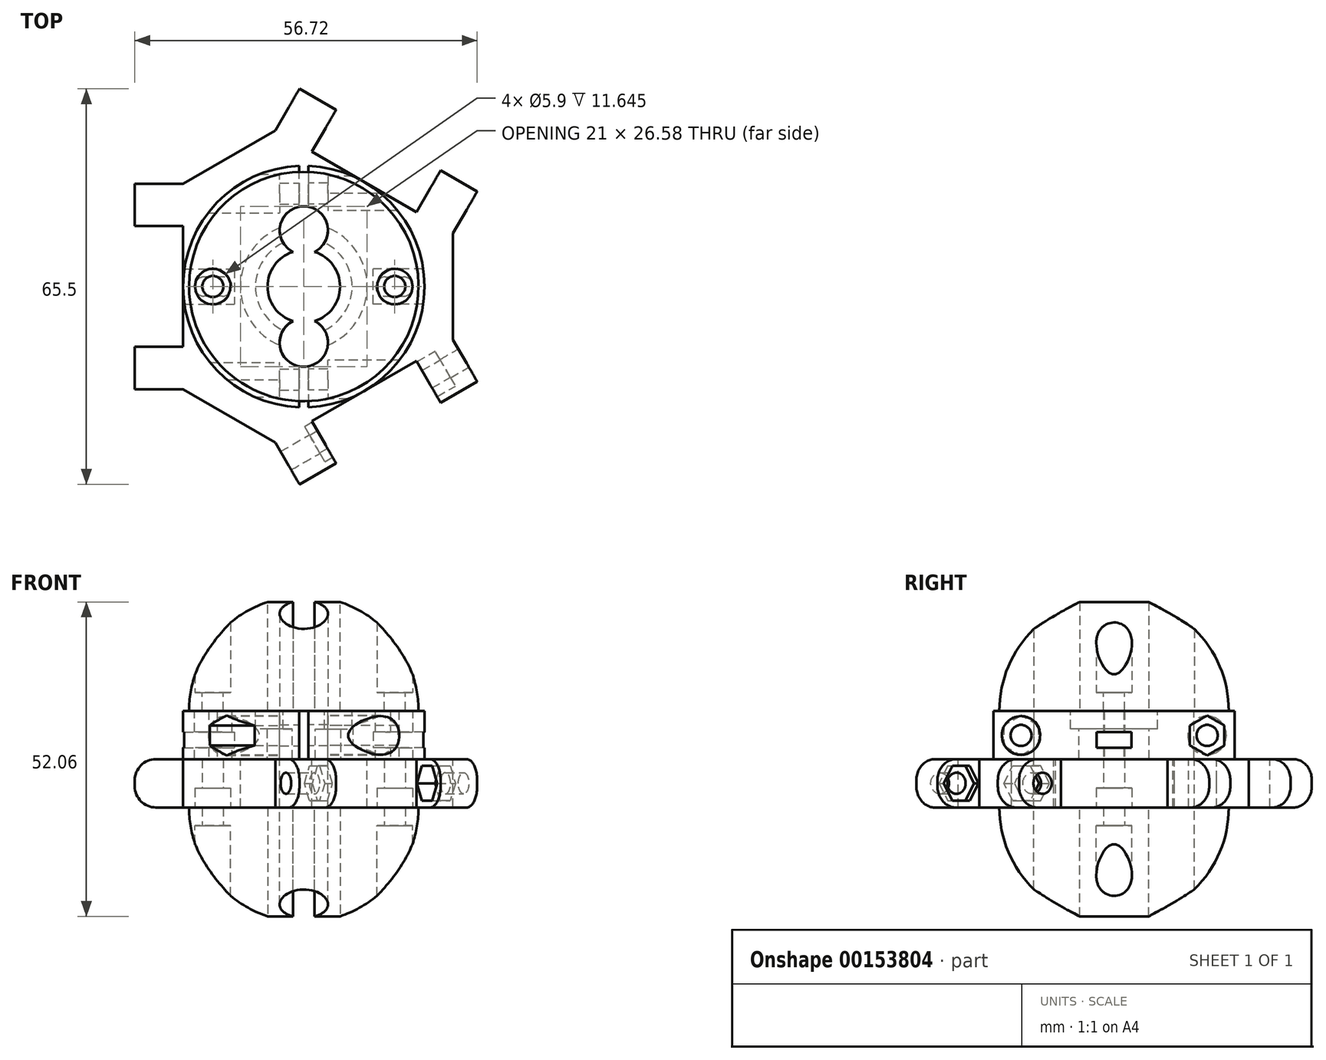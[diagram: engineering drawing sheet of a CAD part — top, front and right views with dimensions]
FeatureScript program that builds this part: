
annotation { "Feature Type Name" : "Feature", "Feature Type Description" : "" }
export const myFeature = defineFeature(function(context is Context, id is Id, definition is map)
    precondition{}
    {
        {
            var Q0;
            Q0=qCreatedBy(makeId("Top.planeOp"),FACE);
            var sketch = newSketch(context, id + "F0", { "sketchPlane" : qUnion([Q0])});
            skArc(sketch, "E0", {"start": v(0.75, -19.99) * mm, "mid": v(20, 0) * mm, "end": v(0.75, 19.99) * mm});
            skArc(sketch, "E1", {"start": v(0.75, -6.05) * mm, "mid": v(6.1, 0) * mm, "end": v(0.75, 6.05) * mm});
            skLineSegment(sketch, "E2", {"start": v(0.75, 19.99) * mm, "end": v(0.75, 6.05) * mm});
            skLineSegment(sketch, "E3.trimOffspring", {"start": v(0.75, -6.05) * mm, "end": v(0.75, -19.99) * mm});
            skSolve(sketch);
        }
        {
            var Q0;
            Q0 = qSketchRegion(id + "F0", true);
            extrude(context, id + "F1", {"entities" : qUnion([Q0]), "depth" : 8 * mm});
        }
        {
            var Q0;
            Q0=qCreatedBy(makeId("Top.planeOp"),FACE);
            cPlane(context, id + "F2", {"entities" : qUnion([Q0]), "cplaneType" : CPlaneType.OFFSET, "offset" : 5 * mm, "width" : 150 * mm, "height" : 150 * mm});
        }
        {
            var Q0;
            Q0=makeQuery(id+"F1.opExtrude","CAP_FACE",FACE,{"disambiguationData":[OSD([sQuery(id+"F0.wireOp",EDGE,"E0"),sQuery(id+"F0.wireOp",EDGE,"E1"),sQuery(id+"F0.wireOp",EDGE,"E2"),sQuery(id+"F0.wireOp",EDGE,"E3.trimOffspring")])],"isStart":false});
            var sketch = newSketch(context, id + "F3", { "sketchPlane" : qUnion([Q0])});
            skCircle(sketch, "E4", {"center": v(0, 0) * mm, "radius": 8 * mm});
            skSolve(sketch);
        }
        {
            var Q0;
            Q0 = qSketchRegion(id + "F3", true);
            var Q1;
            Q1=qCreatedBy(id+"F2.planeOp",FACE);
            extrude(context, id + "F4", {"entities" : qUnion([Q0]), "operationType" : NewBodyOperationType.REMOVE, "endBound" : BoundingType.UP_TO_SURFACE, "oppositeDirection" : true, "endBoundEntityFace" : qUnion([Q1]), "depth" : 25 * mm});
        }
        {
            var Q0;
            Q0=makeQuery(id+"F1.opExtrude","SWEPT_FACE",FACE,{"disambiguationData":[OSD([sQuery(id+"F0.wireOp",EDGE,"E3.trimOffspring")])]});
            var sketch = newSketch(context, id + "F5", { "sketchPlane" : qUnion([Q0])});
            skCircle(sketch, "E5", {"center": v(-15.4, 3.92) * mm, "radius": 1.75 * mm});
            skLineSegment(sketch, "E6", {"start": v(-22.4, 7.85) * mm, "end": v(-22.4, 0) * mm, "construction": true});
            skLineSegment(sketch, "E7", {"start": v(-22.4, 0) * mm, "end": v(-22.4, 3.92) * mm, "construction": true});
            skLineSegment(sketch, "E8", {"start": v(-22.4, 3.92) * mm, "end": v(-12.2, 3.92) * mm, "construction": true});
            skCircle(sketch, "E9.MirrorC", {"center": v(15.4, 3.92) * mm, "radius": 1.75 * mm});
            skSolve(sketch);
        }
        {
            var Q0;
            Q0 = qSketchRegion(id + "F5", true);
            extrude(context, id + "F6", {"entities" : qUnion([Q0]), "operationType" : NewBodyOperationType.REMOVE, "endBound" : BoundingType.UP_TO_NEXT, "oppositeDirection" : true, "depth" : 25 * mm});
        }
        {
            var Q0;
            Q0=qCreatedBy(makeId("Right.planeOp"),FACE);
            cPlane(context, id + "F7", {"entities" : qUnion([Q0]), "cplaneType" : CPlaneType.OFFSET, "offset" : 4 * mm, "width" : 150 * mm, "height" : 150 * mm});
        }
        {
            var Q0;
            Q0=qCreatedBy(id+"F7.planeOp",FACE);
            var sketch = newSketch(context, id + "F8", { "sketchPlane" : qUnion([Q0])});
            skCircle(sketch, "E10.cCircle", {"center": v(15.4, 3.92) * mm, "radius": 3.3 * mm, "construction": true});
            skLineSegment(sketch, "E10.0", {"start": v(12.55, 2.27) * mm, "end": v(12.55, 5.57) * mm});
            skLineSegment(sketch, "E10.1", {"start": v(12.55, 5.57) * mm, "end": v(15.4, 7.22) * mm});
            skLineSegment(sketch, "E10.2", {"start": v(15.4, 7.22) * mm, "end": v(18.27, 5.57) * mm});
            skLineSegment(sketch, "E10.3", {"start": v(18.27, 5.57) * mm, "end": v(18.27, 2.27) * mm});
            skLineSegment(sketch, "E10.4", {"start": v(18.27, 2.27) * mm, "end": v(15.4, 0.62) * mm});
            skLineSegment(sketch, "E10.5", {"start": v(15.4, 0.62) * mm, "end": v(12.55, 2.27) * mm});
            skCircle(sketch, "E11", {"center": v(-15.4, 3.92) * mm, "radius": 3.2 * mm});
            skSolve(sketch);
        }
        {
            var Q0;
            Q0 = qSketchRegion(id + "F8", true);
            var Q1;
            Q1=makeQuery(id+"F1.opExtrude","SWEPT_FACE",FACE,{"disambiguationData":[OSD([sQuery(id+"F0.wireOp",EDGE,"E0")])]});
            extrude(context, id + "F9", {"entities" : qUnion([Q0]), "operationType" : NewBodyOperationType.REMOVE, "endBound" : BoundingType.UP_TO_SURFACE, "endBoundEntityFace" : qUnion([Q1]), "depth" : 25 * mm});
        }
        {
            var Q0;
            {var subQ5=makeQuery(id+"F1.opExtrude","CAP_EDGE",EDGE,{"disambiguationData":[OSD([sQuery(id+"F0.wireOp",EDGE,"E0")])],"isStart":false});Q0=makeQuery(id+"F3.imprint","IMPRINT",FACE,{"disambiguationData":[TD([[makeQuery(id+"F3.imprint","IMPRINT",EDGE,{"derivedFrom":subQ5}),1.0]])]});}
            var sketch = newSketch(context, id + "F10", { "sketchPlane" : qUnion([Q0])});
            skLineSegment(sketch, "E12.bottom", {"start": v(16.5, 1.6) * mm, "end": v(13.5, 1.6) * mm});
            skLineSegment(sketch, "E12.top", {"start": v(16.5, -1.6) * mm, "end": v(13.5, -1.6) * mm});
            skPoint(sketch, "E12.middle", {"position": v(15, 0) * mm});
            skArc(sketch, "E13", {"start": v(16.5, -1.6) * mm, "mid": v(18.1, 0) * mm, "end": v(16.5, 1.6) * mm});
            skArc(sketch, "E14", {"start": v(13.5, 1.6) * mm, "mid": v(11.9, 0) * mm, "end": v(13.5, -1.6) * mm});
            skSolve(sketch);
        }
        {
            var Q0;
            Q0 = qSketchRegion(id + "F10", true);
            extrude(context, id + "F11", {"entities" : qUnion([Q0]), "operationType" : NewBodyOperationType.REMOVE, "endBound" : BoundingType.UP_TO_NEXT, "oppositeDirection" : true, "depth" : 25 * mm});
        }
        {
            var Q0;
            Q0=qCreatedBy(makeId("Right.planeOp"),FACE);
            cPlane(context, id + "F12", {"entities" : qUnion([Q0]), "cplaneType" : CPlaneType.OFFSET, "offset" : 11.5 * mm, "width" : 150 * mm, "height" : 150 * mm});
        }
        {
            var Q0;
            Q0=qCreatedBy(id+"F12.planeOp",FACE);
            var sketch = newSketch(context, id + "F13", { "sketchPlane" : qUnion([Q0])});
            skLineSegment(sketch, "E15.bottom", {"start": v(-2.9, 4.5) * mm, "end": v(2.9, 4.5) * mm});
            skLineSegment(sketch, "E15.top", {"start": v(-2.9, 1.9) * mm, "end": v(2.9, 1.9) * mm});
            skLineSegment(sketch, "E15.left", {"start": v(-2.9, 4.5) * mm, "end": v(-2.9, 1.9) * mm});
            skLineSegment(sketch, "E15.right", {"start": v(2.9, 4.5) * mm, "end": v(2.9, 1.9) * mm});
            skPoint(sketch, "E15.middle", {"position": v(0, 3.2) * mm});
            skSolve(sketch);
        }
        {
            var Q0;
            Q0 = qSketchRegion(id + "F13", true);
            var Q1;
            Q1=makeQuery(id+"F1.opExtrude","SWEPT_FACE",FACE,{"disambiguationData":[OSD([sQuery(id+"F0.wireOp",EDGE,"E0")])]});
            extrude(context, id + "F14", {"entities" : qUnion([Q0]), "operationType" : NewBodyOperationType.REMOVE, "endBound" : BoundingType.UP_TO_SURFACE, "endBoundEntityFace" : qUnion([Q1]), "depth" : 25 * mm});
        }
        {
            var Q0;
            Q0=qCreatedBy(makeId("Right.planeOp"),FACE);
            var sketch = newSketch(context, id + "F15", { "sketchPlane" : qUnion([Q0])});
            skLineSegment(sketch, "E16", {"start": v(0, 0) * mm, "end": v(0, 20.2) * mm, "construction": true});
            skSolve(sketch);
        }
        {
            var Q0;
            Q0=makeQuery(id+"F1.opExtrude","SWEPT_BODY",BODY,{"disambiguationData":[OSD([sQuery(id+"F0.wireOp",EDGE,"E0"),sQuery(id+"F0.wireOp",EDGE,"E1"),sQuery(id+"F0.wireOp",EDGE,"E2"),sQuery(id+"F0.wireOp",EDGE,"E3.trimOffspring")])]});
            var Q1;
            Q1=sQuery(id+"F15.wireOp",EDGE,"E16");
            transform(context, id + "F16", {"entities" : qUnion([Q0]), "transformType" : TransformType.ROTATION, "transformAxis" : qUnion([Q1]), "angle" : 180 * degree, "makeCopy" : true});
        }
        {
            var Q0;
            Q0=makeQuery(id+"F16.opPattern","COPY",FACE,{"derivedFrom":makeQuery(id+"F1.opExtrude","CAP_FACE",FACE,{"disambiguationData":[OSD([sQuery(id+"F0.wireOp",EDGE,"E0"),sQuery(id+"F0.wireOp",EDGE,"E1"),sQuery(id+"F0.wireOp",EDGE,"E2"),sQuery(id+"F0.wireOp",EDGE,"E3.trimOffspring")])],"isStart":true}),"instanceName":"1"});
            var sketch = newSketch(context, id + "F17", { "sketchPlane" : qUnion([Q0])});
            skCircle(sketch, "E17.cCircle", {"center": v(0, 0) * mm, "radius": 24.72 * mm, "construction": true});
            skLineSegment(sketch, "E17.0", {"start": v(17, 20) * mm, "end": v(25.82, 4.72) * mm});
            skLineSegment(sketch, "E17.1", {"start": v(8.82, -24.72) * mm, "end": v(-8.82, -24.72) * mm});
            skLineSegment(sketch, "E17.2", {"start": v(-25.82, 4.72) * mm, "end": v(-17, 20) * mm});
            skPoint(sketch, "E17.0.midPoint", {"position": v(21.41, 12.36) * mm});
            skCircle(sketch, "E18", {"center": v(0, 0) * mm, "radius": 10.5 * mm});
            skLineSegment(sketch, "E19", {"start": v(-10, 20) * mm, "end": v(10, 20) * mm});
            skPoint(sketch, "E20.orphan", {"position": v(0, 49.44) * mm});
            skPoint(sketch, "E21.orphan", {"position": v(42.82, -24.72) * mm});
            skPoint(sketch, "E22.orphan", {"position": v(-42.82, -24.72) * mm});
            skLineSegment(sketch, "E23.top", {"start": v(-17, 28) * mm, "end": v(-10, 28) * mm});
            skLineSegment(sketch, "E23.left", {"start": v(-17, 20) * mm, "end": v(-17, 28) * mm});
            skLineSegment(sketch, "E23.right", {"start": v(-10, 20) * mm, "end": v(-10, 28) * mm});
            skLineSegment(sketch, "E24.top", {"start": v(17, 28) * mm, "end": v(10, 28) * mm});
            skLineSegment(sketch, "E24.left", {"start": v(17, 20) * mm, "end": v(17, 28) * mm});
            skLineSegment(sketch, "E24.right", {"start": v(10, 20) * mm, "end": v(10, 28) * mm});
            skPoint(sketch, "E25.center", {"position": v(0, -1.44) * mm});
            skLineSegment(sketch, "E26.1.0", {"start": v(-8.82, -24.72) * mm, "end": v(-15.75, -28.72) * mm});
            skLineSegment(sketch, "E26.1.1", {"start": v(-15.75, -28.72) * mm, "end": v(-19.25, -22.66) * mm});
            skLineSegment(sketch, "E26.1.2", {"start": v(-12.32, -18.66) * mm, "end": v(-19.25, -22.66) * mm});
            skLineSegment(sketch, "E26.1.3", {"start": v(-22.32, -1.34) * mm, "end": v(-29.25, -5.34) * mm});
            skLineSegment(sketch, "E26.1.4", {"start": v(-32.75, 0.72) * mm, "end": v(-29.25, -5.34) * mm});
            skLineSegment(sketch, "E26.1.5", {"start": v(-25.82, 4.72) * mm, "end": v(-32.75, 0.72) * mm});
            skLineSegment(sketch, "E26.2.0", {"start": v(25.82, 4.72) * mm, "end": v(32.75, 0.72) * mm});
            skLineSegment(sketch, "E26.2.1", {"start": v(32.75, 0.72) * mm, "end": v(29.25, -5.34) * mm});
            skLineSegment(sketch, "E26.2.2", {"start": v(22.32, -1.34) * mm, "end": v(29.25, -5.34) * mm});
            skLineSegment(sketch, "E26.2.3", {"start": v(12.32, -18.66) * mm, "end": v(19.25, -22.66) * mm});
            skLineSegment(sketch, "E26.2.4", {"start": v(15.75, -28.72) * mm, "end": v(19.25, -22.66) * mm});
            skLineSegment(sketch, "E26.2.5", {"start": v(8.82, -24.72) * mm, "end": v(15.75, -28.72) * mm});
            skLineSegment(sketch, "E27.trimOffspring", {"start": v(-22.32, -1.34) * mm, "end": v(-12.32, -18.66) * mm});
            skLineSegment(sketch, "E28.trimOffspring", {"start": v(22.32, -1.34) * mm, "end": v(12.32, -18.66) * mm});
            skSolve(sketch);
        }
        {
            var Q0;
            Q0 = qSketchRegion(id + "F17", true);
            extrude(context, id + "F18", {"entities" : qUnion([Q0]), "depth" : 8 * mm});
        }
        {
            var Q0;
            Q0=makeQuery(id+"F18.opExtrude","CAP_EDGE",EDGE,{"disambiguationData":[OSD([sQuery(id+"F17.wireOp",EDGE,"E26.2.1")])],"isStart":false});
            var Q1;
            Q1=makeQuery(id+"F18.opExtrude","CAP_EDGE",EDGE,{"disambiguationData":[OSD([sQuery(id+"F17.wireOp",EDGE,"E26.2.1")])],"isStart":true});
            var Q2;
            Q2=makeQuery(id+"F18.opExtrude","CAP_EDGE",EDGE,{"disambiguationData":[OSD([sQuery(id+"F17.wireOp",EDGE,"E26.2.4")])],"isStart":false});
            var Q3;
            Q3=makeQuery(id+"F18.opExtrude","CAP_EDGE",EDGE,{"disambiguationData":[OSD([sQuery(id+"F17.wireOp",EDGE,"E26.2.4")])],"isStart":true});
            var Q4;
            Q4=makeQuery(id+"F18.opExtrude","CAP_EDGE",EDGE,{"disambiguationData":[OSD([sQuery(id+"F17.wireOp",EDGE,"E26.1.1")])],"isStart":false});
            var Q5;
            Q5=makeQuery(id+"F18.opExtrude","CAP_EDGE",EDGE,{"disambiguationData":[OSD([sQuery(id+"F17.wireOp",EDGE,"E26.1.1")])],"isStart":true});
            var Q6;
            Q6=makeQuery(id+"F18.opExtrude","CAP_EDGE",EDGE,{"disambiguationData":[OSD([sQuery(id+"F17.wireOp",EDGE,"E26.1.4")])],"isStart":false});
            var Q7;
            Q7=makeQuery(id+"F18.opExtrude","CAP_EDGE",EDGE,{"disambiguationData":[OSD([sQuery(id+"F17.wireOp",EDGE,"E26.1.4")])],"isStart":true});
            var Q8;
            Q8=makeQuery(id+"F18.opExtrude","CAP_EDGE",EDGE,{"disambiguationData":[OSD([sQuery(id+"F17.wireOp",EDGE,"E23.top")])],"isStart":false});
            var Q9;
            Q9=makeQuery(id+"F18.opExtrude","CAP_EDGE",EDGE,{"disambiguationData":[OSD([sQuery(id+"F17.wireOp",EDGE,"E24.top")])],"isStart":false});
            var Q10;
            Q10=makeQuery(id+"F18.opExtrude","CAP_EDGE",EDGE,{"disambiguationData":[OSD([sQuery(id+"F17.wireOp",EDGE,"E23.top")])],"isStart":true});
            var Q11;
            Q11=makeQuery(id+"F18.opExtrude","CAP_EDGE",EDGE,{"disambiguationData":[OSD([sQuery(id+"F17.wireOp",EDGE,"E24.top")])],"isStart":true});
            fillet(context, id + "F19", {"entities" : qUnion([Q0, Q1, Q2, Q3, Q4, Q5, Q6, Q7, Q8, Q9, Q10, Q11]), "radius" : 3.5 * mm, "allowEdgeOverflow" : false});
        }
        {
            var Q0;
            Q0=qCreatedBy(makeId("Front.planeOp"),FACE);
            var sketch = newSketch(context, id + "F20", { "sketchPlane" : qUnion([Q0])});
            skLineSegment(sketch, "E29", {"start": v(0, 0) * mm, "end": v(0, 34.14) * mm, "construction": true});
            skSolve(sketch);
        }
        {
            var Q0;
            Q0=makeQuery(id+"F18.opExtrude","SWEPT_BODY",BODY,{"disambiguationData":[OSD([sQuery(id+"F17.wireOp",EDGE,"E17.0"),sQuery(id+"F17.wireOp",EDGE,"E17.1"),sQuery(id+"F17.wireOp",EDGE,"E17.2"),sQuery(id+"F17.wireOp",EDGE,"E18"),sQuery(id+"F17.wireOp",EDGE,"E19"),sQuery(id+"F17.wireOp",EDGE,"E23.top"),sQuery(id+"F17.wireOp",EDGE,"E23.left"),sQuery(id+"F17.wireOp",EDGE,"E23.right"),sQuery(id+"F17.wireOp",EDGE,"E24.top"),sQuery(id+"F17.wireOp",EDGE,"E24.left"),sQuery(id+"F17.wireOp",EDGE,"E24.right"),sQuery(id+"F17.wireOp",EDGE,"E26.1.0"),sQuery(id+"F17.wireOp",EDGE,"E26.1.1"),sQuery(id+"F17.wireOp",EDGE,"E26.1.2"),sQuery(id+"F17.wireOp",EDGE,"E26.1.3"),sQuery(id+"F17.wireOp",EDGE,"E26.1.4"),sQuery(id+"F17.wireOp",EDGE,"E26.1.5"),sQuery(id+"F17.wireOp",EDGE,"E26.2.0"),sQuery(id+"F17.wireOp",EDGE,"E26.2.1"),sQuery(id+"F17.wireOp",EDGE,"E26.2.2"),sQuery(id+"F17.wireOp",EDGE,"E26.2.3"),sQuery(id+"F17.wireOp",EDGE,"E26.2.4"),sQuery(id+"F17.wireOp",EDGE,"E26.2.5"),sQuery(id+"F17.wireOp",EDGE,"E27.trimOffspring"),sQuery(id+"F17.wireOp",EDGE,"E28.trimOffspring")])]});
            var Q1;
            Q1=sQuery(id+"F20.wireOp",EDGE,"E29");
            transform(context, id + "F21", {"entities" : qUnion([Q0]), "transformType" : TransformType.ROTATION, "transformAxis" : qUnion([Q1]), "angle" : 30 * degree, "makeCopy" : false});
        }
        {
            var Q0;
            Q0=makeQuery(id+"F18.opExtrude","SWEPT_FACE",FACE,{"disambiguationData":[OSD([sQuery(id+"F17.wireOp",EDGE,"E24.left")])]});
            var sketch = newSketch(context, id + "F22", { "sketchPlane" : qUnion([Q0])});
            skPoint(sketch, "E30", {"position": v(-20, -4) * mm});
            skCircle(sketch, "E31", {"center": v(-23.5, -4) * mm, "radius": 1.75 * mm});
            skSolve(sketch);
        }
        {
            var Q0;
            Q0 = qSketchRegion(id + "F22", true);
            var Q1;
            Q1=sQuery(id+"F22.wireOp",EDGE,"E31");
            extrude(context, id + "F23", {"entities" : qUnion([Q0]), "operationType" : NewBodyOperationType.REMOVE, "surfaceEntities" : qUnion([Q1]), "endBound" : BoundingType.THROUGH_ALL, "oppositeDirection" : true, "depth" : 25 * mm});
        }
        {
            var Q0;
            Q0=makeQuery(id+"F18.opExtrude","SWEPT_FACE",FACE,{"disambiguationData":[OSD([sQuery(id+"F17.wireOp",EDGE,"E24.right")])]});
            cPlane(context, id + "F24", {"entities" : qUnion([Q0]), "cplaneType" : CPlaneType.OFFSET, "offset" : 3.5 * mm, "oppositeDirection" : true, "width" : 150 * mm, "height" : 150 * mm});
        }
        {
            var Q0;
            Q0=qCreatedBy(id+"F24.planeOp",FACE);
            var sketch = newSketch(context, id + "F25", { "sketchPlane" : qUnion([Q0])});
            skCircle(sketch, "E32.cCircle", {"center": v(23.5, -4) * mm, "radius": 2.9 * mm, "construction": true});
            skLineSegment(sketch, "E32.0", {"start": v(26.84, -4) * mm, "end": v(25.16, -6.9) * mm});
            skLineSegment(sketch, "E32.1", {"start": v(25.16, -6.9) * mm, "end": v(21.82, -6.9) * mm});
            skLineSegment(sketch, "E32.2", {"start": v(21.82, -6.9) * mm, "end": v(20.14, -4) * mm});
            skLineSegment(sketch, "E32.3", {"start": v(20.14, -4) * mm, "end": v(21.82, -1.1) * mm});
            skLineSegment(sketch, "E32.4", {"start": v(21.82, -1.1) * mm, "end": v(25.16, -1.1) * mm});
            skLineSegment(sketch, "E32.5", {"start": v(25.16, -1.1) * mm, "end": v(26.84, -4) * mm});
            skPoint(sketch, "E32.0.midPoint", {"position": v(26, -5.45) * mm});
            skSolve(sketch);
        }
        {
            var Q0;
            Q0 = qSketchRegion(id + "F25", true);
            extrude(context, id + "F26", {"entities" : qUnion([Q0]), "operationType" : NewBodyOperationType.REMOVE, "depth" : 25 * mm});
        }
        {
            var Q0;
            Q0=makeQuery(id+"F18.opExtrude","CAP_FACE",FACE,{"disambiguationData":[OSD([sQuery(id+"F17.wireOp",EDGE,"E17.0"),sQuery(id+"F17.wireOp",EDGE,"E17.1"),sQuery(id+"F17.wireOp",EDGE,"E17.2"),sQuery(id+"F17.wireOp",EDGE,"E18"),sQuery(id+"F17.wireOp",EDGE,"E19"),sQuery(id+"F17.wireOp",EDGE,"E23.top"),sQuery(id+"F17.wireOp",EDGE,"E23.left"),sQuery(id+"F17.wireOp",EDGE,"E23.right"),sQuery(id+"F17.wireOp",EDGE,"E24.top"),sQuery(id+"F17.wireOp",EDGE,"E24.left"),sQuery(id+"F17.wireOp",EDGE,"E24.right"),sQuery(id+"F17.wireOp",EDGE,"E26.1.0"),sQuery(id+"F17.wireOp",EDGE,"E26.1.1"),sQuery(id+"F17.wireOp",EDGE,"E26.1.2"),sQuery(id+"F17.wireOp",EDGE,"E26.1.3"),sQuery(id+"F17.wireOp",EDGE,"E26.1.4"),sQuery(id+"F17.wireOp",EDGE,"E26.1.5"),sQuery(id+"F17.wireOp",EDGE,"E26.2.0"),sQuery(id+"F17.wireOp",EDGE,"E26.2.1"),sQuery(id+"F17.wireOp",EDGE,"E26.2.2"),sQuery(id+"F17.wireOp",EDGE,"E26.2.3"),sQuery(id+"F17.wireOp",EDGE,"E26.2.4"),sQuery(id+"F17.wireOp",EDGE,"E26.2.5"),sQuery(id+"F17.wireOp",EDGE,"E27.trimOffspring"),sQuery(id+"F17.wireOp",EDGE,"E28.trimOffspring")])],"isStart":false});
            var sketch = newSketch(context, id + "F27", { "sketchPlane" : qUnion([Q0])});
            skPoint(sketch, "E33", {"position": v(-15.06, 0) * mm});
            skPoint(sketch, "E34.MirrorP", {"position": v(15.06, 0) * mm});
            skSolve(sketch);
        }
        {
            var Q0;
            Q0=sQuery(id+"F27.wireOp",VERTEX,"E34.MirrorP");
            var Q1;
            Q1=sQuery(id+"F27.wireOp",VERTEX,"E33");
            var Q2;
            Q2=makeQuery(id+"F18.opExtrude","SWEPT_BODY",BODY,{"disambiguationData":[OSD([sQuery(id+"F17.wireOp",EDGE,"E17.0"),sQuery(id+"F17.wireOp",EDGE,"E17.1"),sQuery(id+"F17.wireOp",EDGE,"E17.2"),sQuery(id+"F17.wireOp",EDGE,"E18"),sQuery(id+"F17.wireOp",EDGE,"E19"),sQuery(id+"F17.wireOp",EDGE,"E23.top"),sQuery(id+"F17.wireOp",EDGE,"E23.left"),sQuery(id+"F17.wireOp",EDGE,"E23.right"),sQuery(id+"F17.wireOp",EDGE,"E24.top"),sQuery(id+"F17.wireOp",EDGE,"E24.left"),sQuery(id+"F17.wireOp",EDGE,"E24.right"),sQuery(id+"F17.wireOp",EDGE,"E26.1.0"),sQuery(id+"F17.wireOp",EDGE,"E26.1.1"),sQuery(id+"F17.wireOp",EDGE,"E26.1.2"),sQuery(id+"F17.wireOp",EDGE,"E26.1.3"),sQuery(id+"F17.wireOp",EDGE,"E26.1.4"),sQuery(id+"F17.wireOp",EDGE,"E26.1.5"),sQuery(id+"F17.wireOp",EDGE,"E26.2.0"),sQuery(id+"F17.wireOp",EDGE,"E26.2.1"),sQuery(id+"F17.wireOp",EDGE,"E26.2.2"),sQuery(id+"F17.wireOp",EDGE,"E26.2.3"),sQuery(id+"F17.wireOp",EDGE,"E26.2.4"),sQuery(id+"F17.wireOp",EDGE,"E26.2.5"),sQuery(id+"F17.wireOp",EDGE,"E27.trimOffspring"),sQuery(id+"F17.wireOp",EDGE,"E28.trimOffspring")])]});
            hole(context, id + "F28", {"style" : HoleStyle.C_BORE, "endStyle" : HoleEndStyle.THROUGH, "holeDiameter" : 3.5 * mm, "cBoreDiameter" : 5.9 * mm, "cBoreDepth" : 3.2 * mm, "locations" : qUnion([Q0, Q1]), "scope" : qUnion([Q2]), "isTappedThrough" : true});
        }
        {
            var Q0;
            Q0=sQuery(id+"F20.wireOp",EDGE,"E29");
            cPlane(context, id + "F29", {"entities" : qUnion([Q0]), "cplaneType" : CPlaneType.LINE_ANGLE, "offset" : 25 * mm, "angle" : 0 * degree, "width" : 150 * mm, "height" : 150 * mm});
        }
        {
            var Q0;
            Q0=qCreatedBy(id+"F29.planeOp",FACE);
            var sketch = newSketch(context, id + "F30", { "sketchPlane" : qUnion([Q0])});
            skPoint(sketch, "E35", {"position": v(-19, -8) * mm});
            skArc(sketch, "E36", {"start": v(-19, -8) * mm, "mid": v(-15.41, -19.11) * mm, "end": v(-6, -26.03) * mm});
            skLineSegment(sketch, "E37", {"start": v(-19, -8) * mm, "end": v(-6, -8) * mm});
            skLineSegment(sketch, "E38", {"start": v(-6, -8) * mm, "end": v(-6, -26.03) * mm});
            skSolve(sketch);
        }
        {
            var Q0;
            Q0 = qSketchRegion(id + "F30", true);
            var Q1;
            Q1=sQuery(id+"F20.wireOp",EDGE,"E29");
            revolve(context, id + "F31", {"entities" : qUnion([Q0]), "axis" : qUnion([Q1]), "revolveType" : RevolveType.FULL});
        }
        {
            var Q0;
            {var subQ5=makeQuery(id+"F1.opExtrude","CAP_EDGE",EDGE,{"disambiguationData":[OSD([sQuery(id+"F0.wireOp",EDGE,"E1")])],"isStart":false});Q0=makeQuery(id+"F3.imprint","IMPRINT",FACE,{"disambiguationData":[TD([[makeQuery(id+"F3.imprint","IMPRINT",EDGE,{"derivedFrom":subQ5}),1.0]])]});}
            var sketch = newSketch(context, id + "F32", { "sketchPlane" : qUnion([Q0])});
            skCircle(sketch, "E39", {"center": v(0, 9.3) * mm, "radius": 4 * mm});
            skLineSegment(sketch, "E40", {"start": v(0, 0) * mm, "end": v(-36.82, 0) * mm, "construction": true});
            skCircle(sketch, "E41.MirrorC", {"center": v(0, -9.3) * mm, "radius": 4 * mm});
            skSolve(sketch);
        }
        {
            var Q0;
            Q0 = qSketchRegion(id + "F32", true);
            extrude(context, id + "F33", {"entities" : qUnion([Q0]), "operationType" : NewBodyOperationType.REMOVE, "endBound" : BoundingType.THROUGH_ALL, "oppositeDirection" : true, "depth" : 25 * mm});
        }
        {
            var Q0;
            Q0=makeQuery(id+"F18.opExtrude","CAP_FACE",FACE,{"disambiguationData":[OSD([sQuery(id+"F17.wireOp",EDGE,"E17.0"),sQuery(id+"F17.wireOp",EDGE,"E17.1"),sQuery(id+"F17.wireOp",EDGE,"E17.2"),sQuery(id+"F17.wireOp",EDGE,"E18"),sQuery(id+"F17.wireOp",EDGE,"E19"),sQuery(id+"F17.wireOp",EDGE,"E23.top"),sQuery(id+"F17.wireOp",EDGE,"E23.left"),sQuery(id+"F17.wireOp",EDGE,"E23.right"),sQuery(id+"F17.wireOp",EDGE,"E24.top"),sQuery(id+"F17.wireOp",EDGE,"E24.left"),sQuery(id+"F17.wireOp",EDGE,"E24.right"),sQuery(id+"F17.wireOp",EDGE,"E26.1.0"),sQuery(id+"F17.wireOp",EDGE,"E26.1.1"),sQuery(id+"F17.wireOp",EDGE,"E26.1.2"),sQuery(id+"F17.wireOp",EDGE,"E26.1.3"),sQuery(id+"F17.wireOp",EDGE,"E26.1.4"),sQuery(id+"F17.wireOp",EDGE,"E26.1.5"),sQuery(id+"F17.wireOp",EDGE,"E26.2.0"),sQuery(id+"F17.wireOp",EDGE,"E26.2.1"),sQuery(id+"F17.wireOp",EDGE,"E26.2.2"),sQuery(id+"F17.wireOp",EDGE,"E26.2.3"),sQuery(id+"F17.wireOp",EDGE,"E26.2.4"),sQuery(id+"F17.wireOp",EDGE,"E26.2.5"),sQuery(id+"F17.wireOp",EDGE,"E27.trimOffspring"),sQuery(id+"F17.wireOp",EDGE,"E28.trimOffspring")])],"isStart":false});
            cPlane(context, id + "F34", {"entities" : qUnion([Q0]), "cplaneType" : CPlaneType.OFFSET, "offset" : 3 * mm, "width" : 150 * mm, "height" : 150 * mm});
        }
        {
            var Q0;
            Q0=qCreatedBy(id+"F34.planeOp",FACE);
            var sketch = newSketch(context, id + "F35", { "sketchPlane" : qUnion([Q0])});
            skCircle(sketch, "E42", {"center": v(-15.06, 0) * mm, "radius": 1.75 * mm});
            skCircle(sketch, "E43.MirrorC", {"center": v(15.06, 0) * mm, "radius": 1.75 * mm});
            skSolve(sketch);
        }
        {
            var Q0;
            Q0 = qSketchRegion(id + "F35", true);
            extrude(context, id + "F36", {"entities" : qUnion([Q0]), "operationType" : NewBodyOperationType.REMOVE, "endBound" : BoundingType.THROUGH_ALL, "oppositeDirection" : true, "depth" : 25 * mm});
        }
        {
            var Q0;
            Q0=qCreatedBy(id+"F34.planeOp",FACE);
            var sketch = newSketch(context, id + "F37", { "sketchPlane" : qUnion([Q0])});
            skCircle(sketch, "E44", {"center": v(-15.06, 0) * mm, "radius": 2.95 * mm});
            skCircle(sketch, "E45.MirrorC", {"center": v(15.06, 0) * mm, "radius": 2.95 * mm});
            skSolve(sketch);
        }
        {
            var Q0;
            Q0 = qSketchRegion(id + "F37", true);
            var Q1;
            Q1=makeQuery(id+"F31.opRevolve","SWEPT_FACE",FACE,{"disambiguationData":[OSD([sQuery(id+"F30.wireOp",EDGE,"E36")])]});
            extrude(context, id + "F38", {"entities" : qUnion([Q0]), "operationType" : NewBodyOperationType.REMOVE, "endBoundEntityFace" : qUnion([Q1]), "depth" : 25 * mm});
        }
        {
            var Q0;
            Q0=makeQuery(id+"F31.opRevolve","SWEPT_BODY",BODY,{"disambiguationData":[OSD([sQuery(id+"F30.wireOp",EDGE,"E36"),sQuery(id+"F30.wireOp",EDGE,"E37"),sQuery(id+"F30.wireOp",EDGE,"E38")])]});
            var Q1;
            Q1=makeQuery(id+"F18.opExtrude","CAP_FACE",FACE,{"disambiguationData":[OSD([sQuery(id+"F17.wireOp",EDGE,"E17.0"),sQuery(id+"F17.wireOp",EDGE,"E17.1"),sQuery(id+"F17.wireOp",EDGE,"E17.2"),sQuery(id+"F17.wireOp",EDGE,"E18"),sQuery(id+"F17.wireOp",EDGE,"E19"),sQuery(id+"F17.wireOp",EDGE,"E23.top"),sQuery(id+"F17.wireOp",EDGE,"E23.left"),sQuery(id+"F17.wireOp",EDGE,"E23.right"),sQuery(id+"F17.wireOp",EDGE,"E24.top"),sQuery(id+"F17.wireOp",EDGE,"E24.left"),sQuery(id+"F17.wireOp",EDGE,"E24.right"),sQuery(id+"F17.wireOp",EDGE,"E26.1.0"),sQuery(id+"F17.wireOp",EDGE,"E26.1.1"),sQuery(id+"F17.wireOp",EDGE,"E26.1.2"),sQuery(id+"F17.wireOp",EDGE,"E26.1.3"),sQuery(id+"F17.wireOp",EDGE,"E26.1.4"),sQuery(id+"F17.wireOp",EDGE,"E26.1.5"),sQuery(id+"F17.wireOp",EDGE,"E26.2.0"),sQuery(id+"F17.wireOp",EDGE,"E26.2.1"),sQuery(id+"F17.wireOp",EDGE,"E26.2.2"),sQuery(id+"F17.wireOp",EDGE,"E26.2.3"),sQuery(id+"F17.wireOp",EDGE,"E26.2.4"),sQuery(id+"F17.wireOp",EDGE,"E26.2.5"),sQuery(id+"F17.wireOp",EDGE,"E27.trimOffspring"),sQuery(id+"F17.wireOp",EDGE,"E28.trimOffspring")])],"isStart":true});
            mirror(context, id + "F39", {"entities" : qUnion([Q0]), "mirrorPlane" : qUnion([Q1])});
        }
    });
